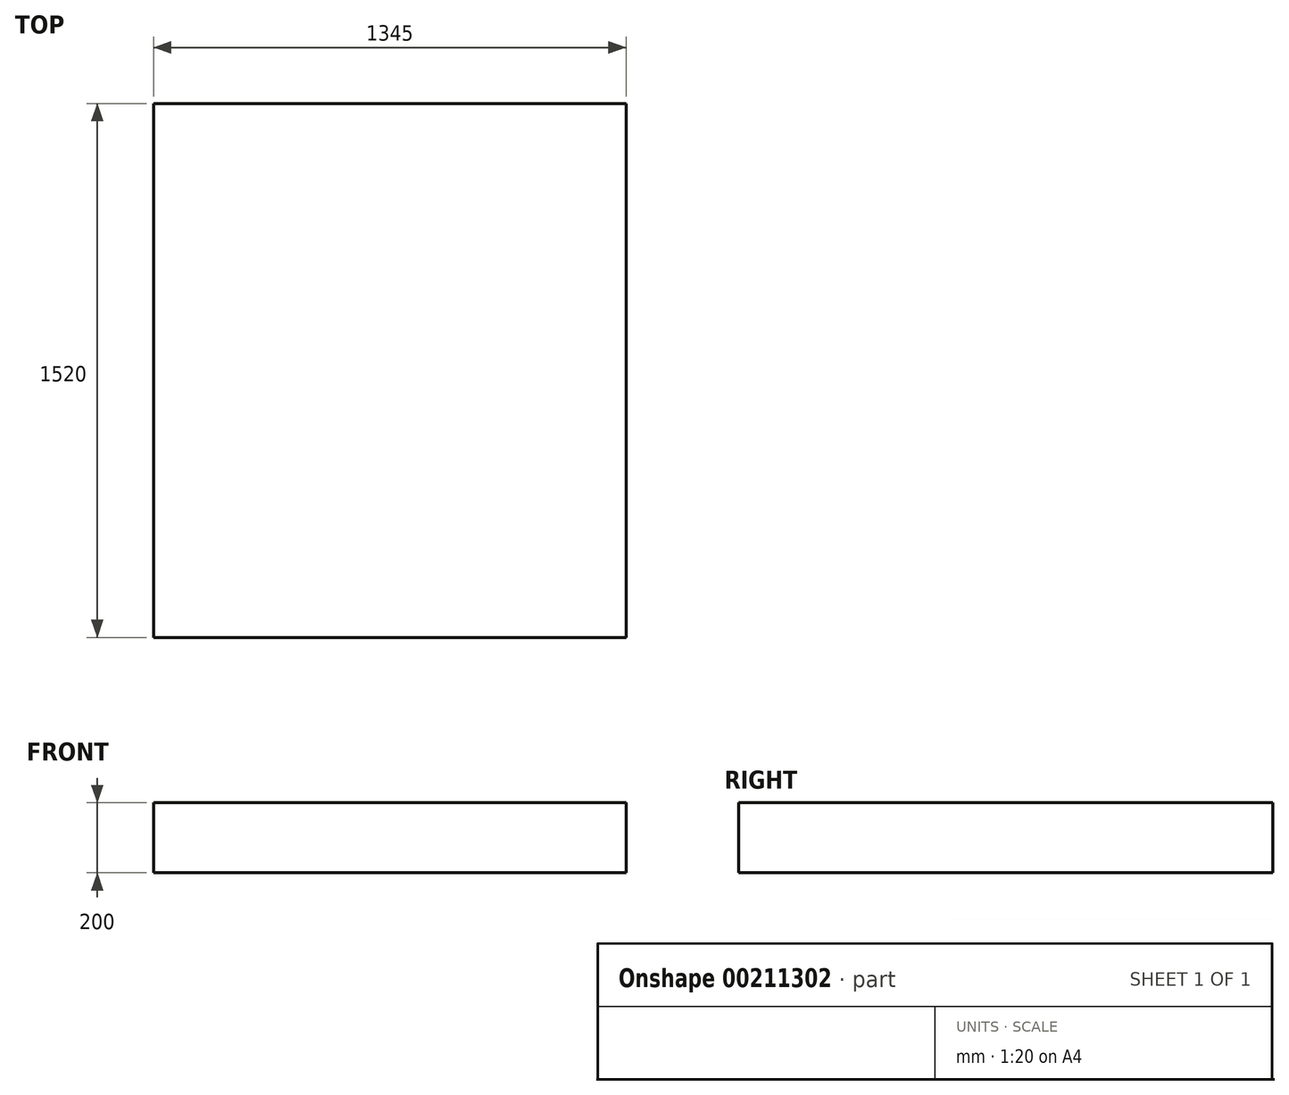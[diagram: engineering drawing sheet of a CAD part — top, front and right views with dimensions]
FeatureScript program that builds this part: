
annotation { "Feature Type Name" : "Feature", "Feature Type Description" : "" }
export const myFeature = defineFeature(function(context is Context, id is Id, definition is map)
    precondition{}
    {
        {
            var Q0;
            Q0=qCreatedBy(makeId("Top.planeOp"),FACE);
            var sketch = newSketch(context, id + "F0", { "sketchPlane" : qUnion([Q0])});
            skLineSegment(sketch, "E0.bottom", {"start": v(-675.9, 1024.83) * mm, "end": v(669.1, 1024.83) * mm});
            skLineSegment(sketch, "E0.top", {"start": v(-675.9, -495.17) * mm, "end": v(669.1, -495.17) * mm});
            skLineSegment(sketch, "E0.left", {"start": v(-675.9, 1024.83) * mm, "end": v(-675.9, -495.17) * mm});
            skLineSegment(sketch, "E0.right", {"start": v(669.1, 1024.83) * mm, "end": v(669.1, -495.17) * mm});
            skSolve(sketch);
        }
        {
            var Q0;
            Q0=makeQuery(id+"F0.imprint","IMPRINT",FACE,{"disambiguationData":[TD([[makeQuery(id+"F0.imprint","IMPRINT",EDGE,{"derivedFrom":sQuery(id+"F0.wireOp",EDGE,"E0.bottom")}),-1.0]])]});
            extrude(context, id + "F1", {"entities" : qUnion([Q0]), "depth" : 200 * mm});
        }
    });
